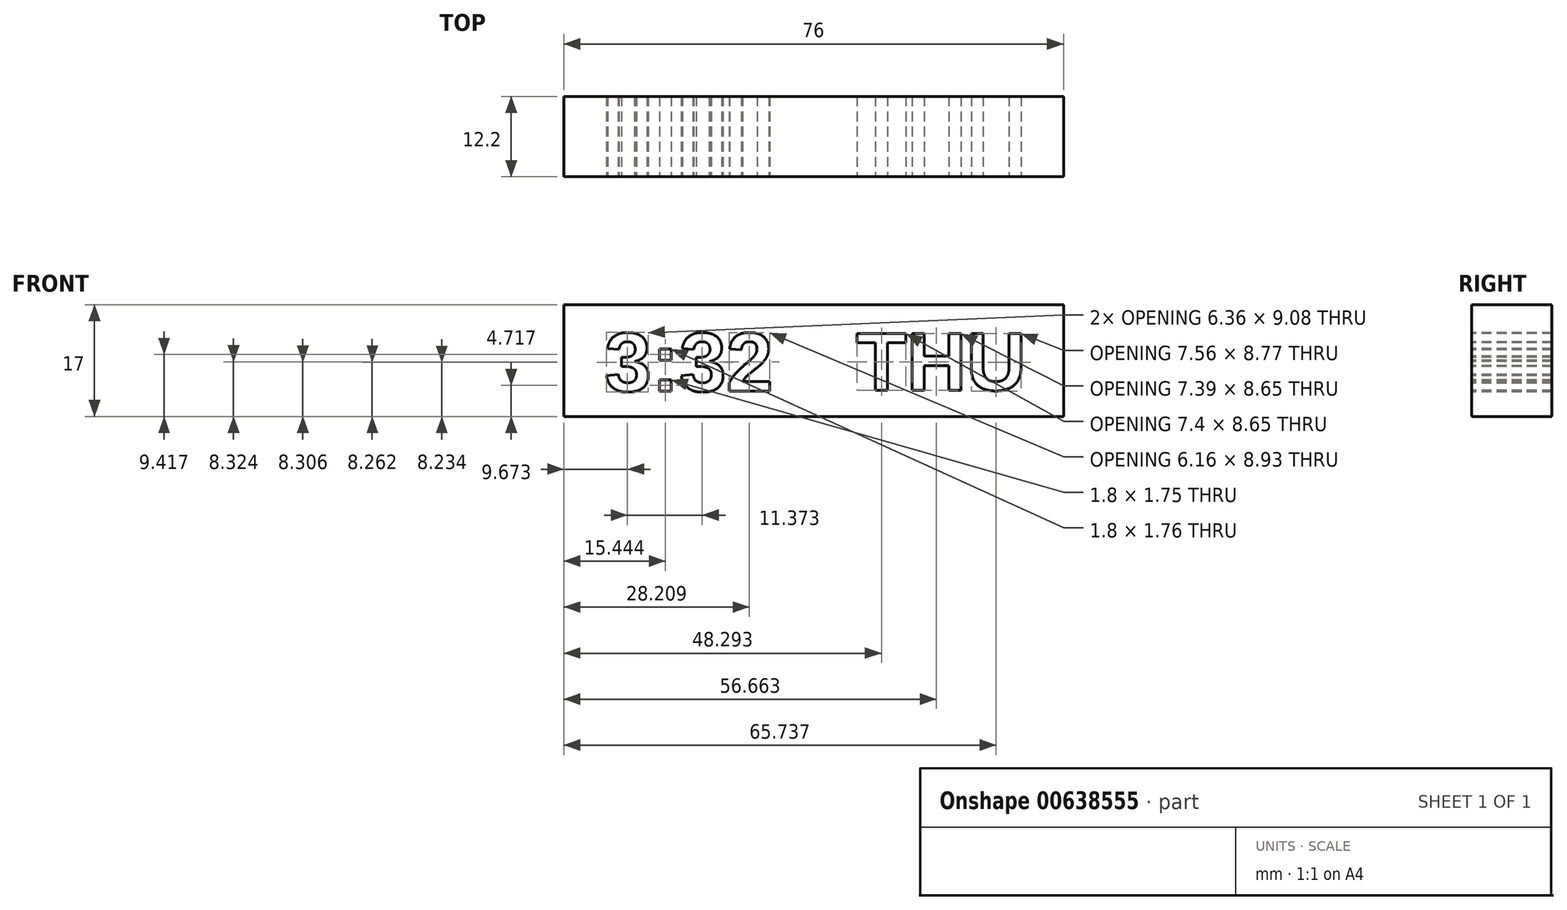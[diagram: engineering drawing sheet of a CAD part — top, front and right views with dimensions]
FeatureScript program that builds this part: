
annotation { "Feature Type Name" : "Feature", "Feature Type Description" : "" }
export const myFeature = defineFeature(function(context is Context, id is Id, definition is map)
    precondition{}
    {
        {
            var Q0;
            Q0=qCreatedBy(makeId("Front.planeOp"),FACE);
            var sketch = newSketch(context, id + "F0", { "sketchPlane" : qUnion([Q0])});
            skLineSegment(sketch, "E0.bottom", {"start": v(-38.28, 3.95) * mm, "end": v(37.72, 3.95) * mm});
            skLineSegment(sketch, "E0.top", {"start": v(-38.28, -13.05) * mm, "end": v(37.72, -13.05) * mm});
            skLineSegment(sketch, "E0.left", {"start": v(-38.28, 3.95) * mm, "end": v(-38.28, -13.05) * mm});
            skLineSegment(sketch, "E0.right", {"start": v(37.72, 3.95) * mm, "end": v(37.72, -13.05) * mm});
            skText(sketch, "E1", { "text": "3:32", "fontName": "Arimo-Bold.ttf"});
            skText(sketch, "E2", { "text": "THU", "fontName": "Arimo-Bold.ttf"});
            skLineSegment(sketch, "E3", {"start": v(0, 3.95) * mm, "end": v(0, -13.05) * mm});
            const initialGuessF0  = {"E1": [-0.03208, -0.00921, 1, 0, 0.00921], "E2": [0.00617, -0.00905, 1, 0, 0.00905]};
            skSetInitialGuess(sketch, initialGuessF0);
            skSolve(sketch);
        }
        {
            var Q0;
            {var subQ0=sQuery(id+"F0.wireOp",EDGE,"E0.right");Q0=makeQuery(id+"F0.imprint","IMPRINT",FACE,{"disambiguationData":[TD([[makeQuery(id+"F0.imprint","IMPRINT",EDGE,{"derivedFrom":subQ0}),-1.0]])]});}
            var Q1;
            {var subQ1=sQuery(id+"F0.wireOp",EDGE,"E0.left");Q1=makeQuery(id+"F0.imprint","IMPRINT",FACE,{"disambiguationData":[TD([[makeQuery(id+"F0.imprint","IMPRINT",EDGE,{"derivedFrom":subQ1}),1.0]])]});}
            extrude(context, id + "F1", {"entities" : qUnion([Q0, Q1]), "oppositeDirection" : true, "depth" : 12.2 * mm, "offsetDistance" : 25 * mm});
        }
    });
